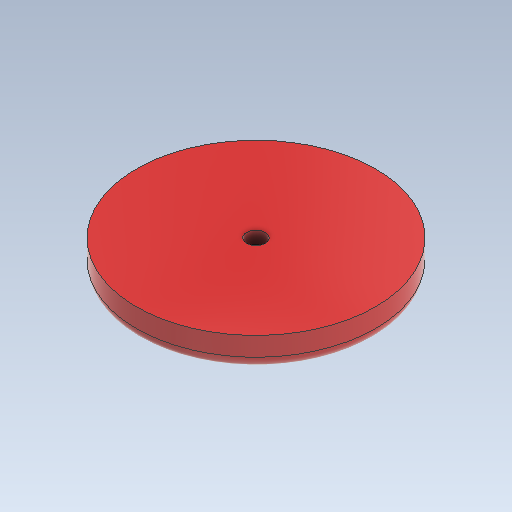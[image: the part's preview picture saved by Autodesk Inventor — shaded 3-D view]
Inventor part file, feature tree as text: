
AUTODESK INVENTOR PART (.ipt)
format: ipt  version: 2020 (Build 240168000, 168)  size: 157,696 bytes
history: native  units: mm
features: fillet x2, revolve x1, sketch x1
ambient origin geometry x8: Origin, YZ Plane, XZ Plane, XY Plane, X Axis, Y Axis, Z Axis, Center Point
bodies: Solid1 (feature_tree)
feature tree (4):
  revolve  "Revolution1"  [1 undecoded]
  fillet  "Fillet2"  Radius=5.0mm
  fillet  "Fillet3"  Radius=1.5mm
  sketch  "Sketch1"  dims[d5=19.0mm d12=2.0mm d16=5.0mm d17=1.5mm d18=90.0deg d23=2.0mm d24=90.0deg d25=4.0mm d26=0.5mm d27=2.0mm]
note: 1 required parameter value undecoded (feature->parameter linkage not recoverable at this tier; creation-order binding heuristic only, values carry confidence <= 0.55)
